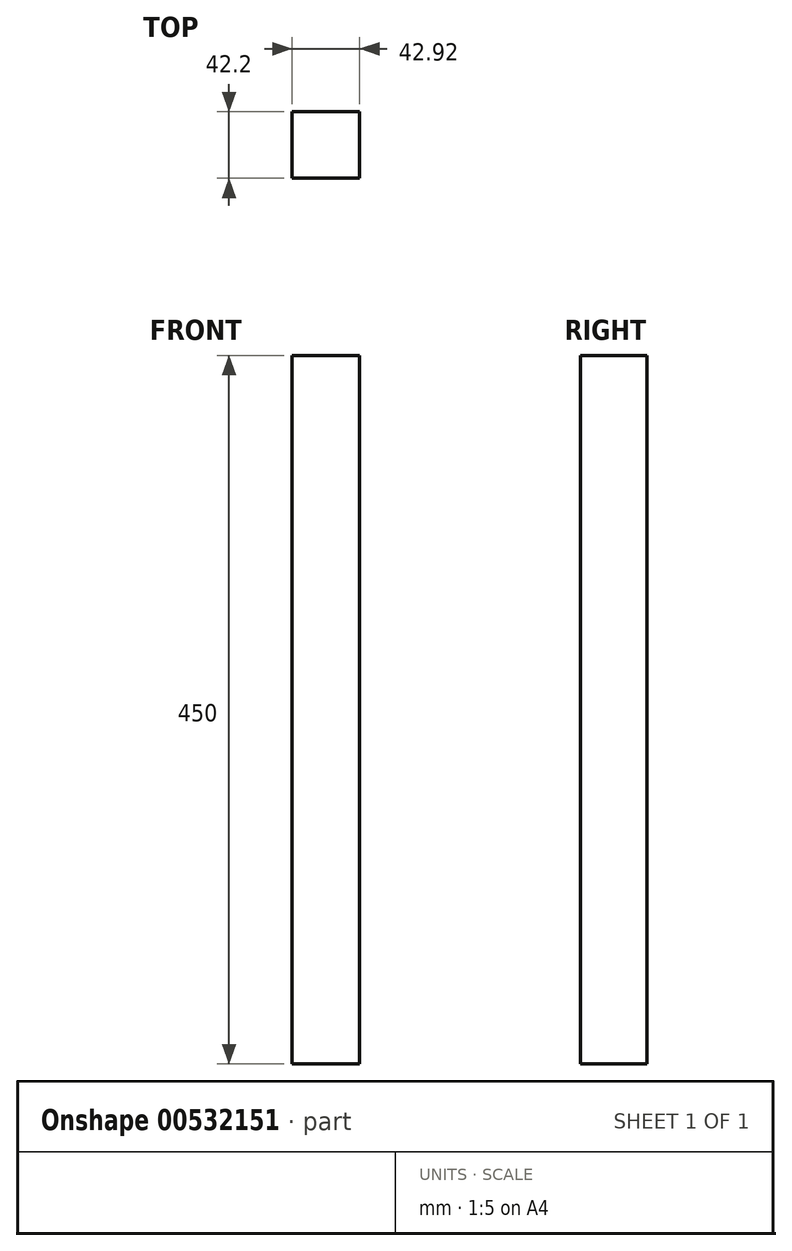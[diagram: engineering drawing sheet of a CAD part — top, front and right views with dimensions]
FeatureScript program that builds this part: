
annotation { "Feature Type Name" : "Feature", "Feature Type Description" : "" }
export const myFeature = defineFeature(function(context is Context, id is Id, definition is map)
    precondition{}
    {
        {
            var Q0;
            Q0=qCreatedBy(makeId("Top.planeOp"),FACE);
            var sketch = newSketch(context, id + "F0", { "sketchPlane" : qUnion([Q0])});
            skLineSegment(sketch, "E0", {"start": v(0, 0) * mm, "end": v(-42.92, 0) * mm});
            skLineSegment(sketch, "E1", {"start": v(-42.92, 0) * mm, "end": v(-42.92, 42.2) * mm});
            skLineSegment(sketch, "E2", {"start": v(-42.92, 42.2) * mm, "end": v(0, 42.2) * mm});
            skLineSegment(sketch, "E3", {"start": v(0, 0) * mm, "end": v(0, 42.2) * mm});
            skSolve(sketch);
        }
        {
            var Q0;
            Q0 = qSketchRegion(id + "F0", true);
            extrude(context, id + "F1", {"entities" : qUnion([Q0]), "depth" : 450 * mm, "offsetDistance" : 25 * mm});
        }
    });
